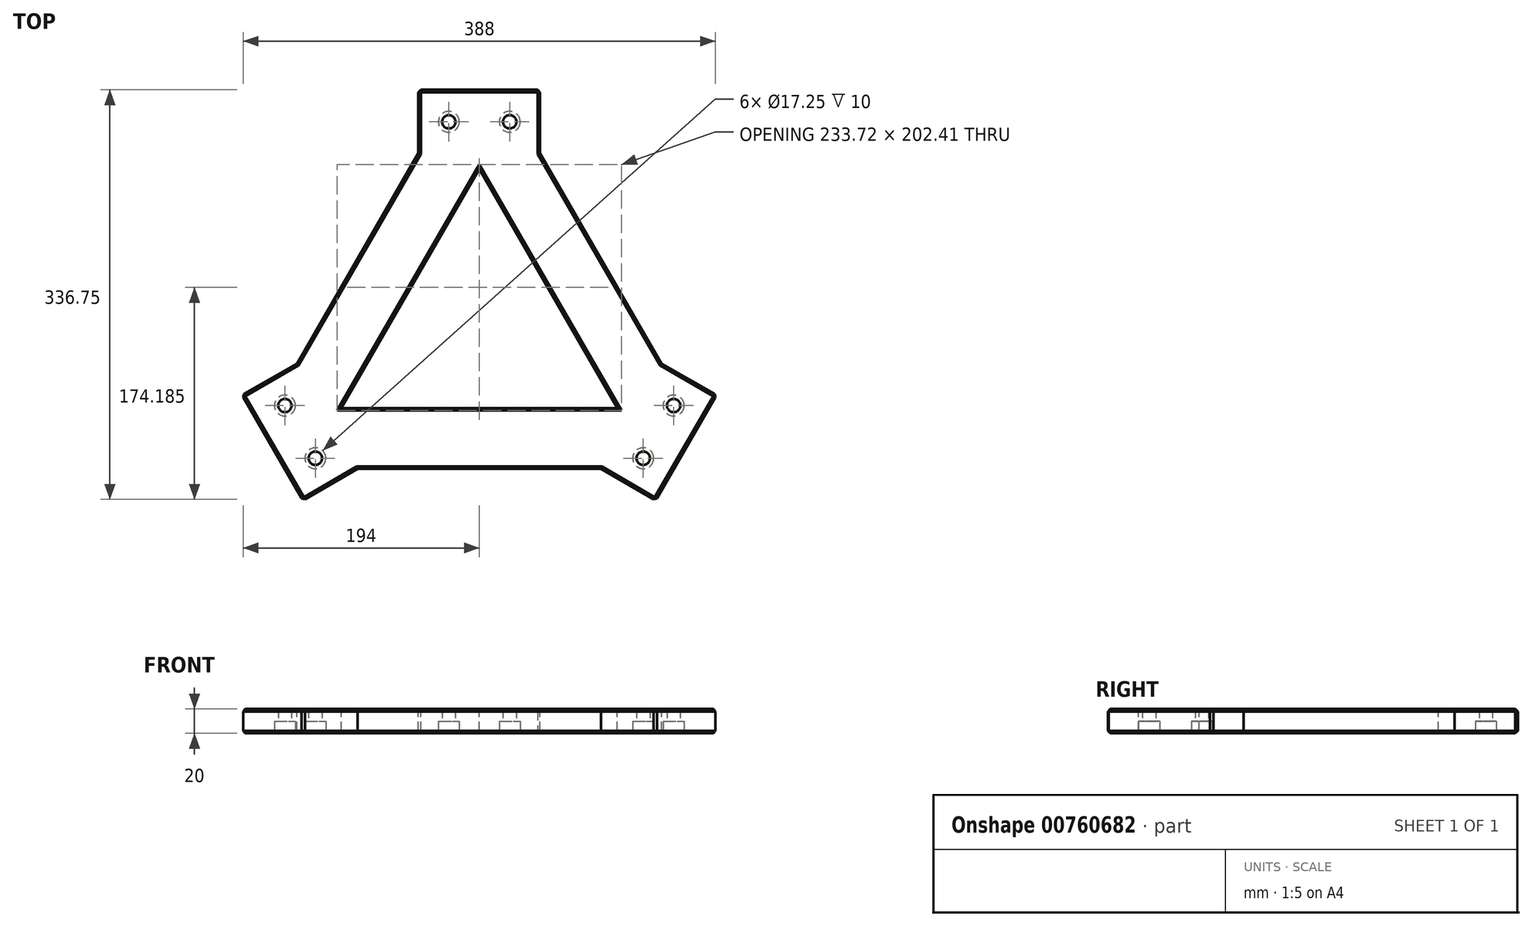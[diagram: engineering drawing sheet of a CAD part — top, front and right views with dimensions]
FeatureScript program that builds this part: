
annotation { "Feature Type Name" : "Feature", "Feature Type Description" : "" }
export const myFeature = defineFeature(function(context is Context, id is Id, definition is map)
    precondition{}
    {
        {
            var Q0;
            Q0=qCreatedBy(makeId("Top.planeOp"),FACE);
            var sketch = newSketch(context, id + "F0", { "sketchPlane" : qUnion([Q0])});
            skLineSegment(sketch, "E0", {"start": v(-200, -115.47) * mm, "end": v(200, -115.47) * mm});
            skLineSegment(sketch, "E1", {"start": v(200, -115.47) * mm, "end": v(0, 230.94) * mm});
            skLineSegment(sketch, "E2", {"start": v(0, 230.94) * mm, "end": v(-200, -115.47) * mm});
            skLineSegment(sketch, "E3", {"start": v(-200, -115.47) * mm, "end": v(100, 57.74) * mm, "construction": true});
            skLineSegment(sketch, "E4", {"start": v(0, 230.94) * mm, "end": v(0, -115.47) * mm, "construction": true});
            skPoint(sketch, "E5", {"position": v(0, 0) * mm});
            skLineSegment(sketch, "E6.0", {"start": v(0, 130.94) * mm, "end": v(-113.4, -65.47) * mm});
            skLineSegment(sketch, "E6.1", {"start": v(113.4, -65.47) * mm, "end": v(0, 130.94) * mm});
            skLineSegment(sketch, "E6.2", {"start": v(-113.4, -65.47) * mm, "end": v(113.4, -65.47) * mm});
            skSolve(sketch);
        }
        {
            var Q0;
            Q0=makeQuery(id+"F0.imprint","IMPRINT",FACE,{"disambiguationData":[TD([[makeQuery(id+"F0.imprint","IMPRINT",EDGE,{"derivedFrom":sQuery(id+"F0.wireOp",EDGE,"E0")}),1.0]])]});
            extrude(context, id + "F1", {"entities" : qUnion([Q0]), "oppositeDirection" : true, "depth" : 20 * mm, "offsetDistance" : 25 * mm});
        }
        {
            var Q0;
            Q0=makeQuery(id+"F1.opExtrude","SWEPT_EDGE",EDGE,{"disambiguationData":[OSD([sQuery(id+"F0.wireOp",EDGE,"E0"),sQuery(id+"F0.wireOp",EDGE,"E2")])]});
            var Q1;
            Q1=makeQuery(id+"F1.opExtrude","SWEPT_EDGE",EDGE,{"disambiguationData":[OSD([sQuery(id+"F0.wireOp",EDGE,"E0"),sQuery(id+"F0.wireOp",EDGE,"E1")])]});
            var Q2;
            Q2=makeQuery(id+"F1.opExtrude","SWEPT_EDGE",EDGE,{"disambiguationData":[OSD([sQuery(id+"F0.wireOp",EDGE,"E1"),sQuery(id+"F0.wireOp",EDGE,"E2")])]});
            chamfer(context, id + "F2", {"entities" : qUnion([Q0, Q1, Q2]), "width" : 40 * mm, "tangentPropagation" : true});
        }
        {
            var Q0;
            Q0=makeQuery(id+"F1.opExtrude","CAP_FACE",FACE,{"disambiguationData":[OSD([sQuery(id+"F0.wireOp",EDGE,"E0"),sQuery(id+"F0.wireOp",EDGE,"E1"),sQuery(id+"F0.wireOp",EDGE,"E2"),sQuery(id+"F0.wireOp",EDGE,"E6.0"),sQuery(id+"F0.wireOp",EDGE,"E6.1"),sQuery(id+"F0.wireOp",EDGE,"E6.2")])],"isStart":true});
            var sketch = newSketch(context, id + "F3", { "sketchPlane" : qUnion([Q0])});
            skLineSegment(sketch, "E7.bottom", {"start": v(-50, 196.3) * mm, "end": v(50, 196.3) * mm});
            skLineSegment(sketch, "E7.top", {"start": v(-50, 144.34) * mm, "end": v(50, 144.34) * mm});
            skLineSegment(sketch, "E7.left", {"start": v(-50, 144.34) * mm, "end": v(-50, 196.3) * mm});
            skLineSegment(sketch, "E7.right", {"start": v(50, 144.34) * mm, "end": v(50, 196.3) * mm});
            skLineSegment(sketch, "E8.1.0", {"start": v(-100, -115.47) * mm, "end": v(-145, -141.45) * mm});
            skLineSegment(sketch, "E8.1.1", {"start": v(-150, -28.87) * mm, "end": v(-195, -54.85) * mm});
            skLineSegment(sketch, "E8.1.2", {"start": v(-100, -115.47) * mm, "end": v(-150, -28.87) * mm});
            skLineSegment(sketch, "E8.1.3", {"start": v(-145, -141.45) * mm, "end": v(-195, -54.85) * mm});
            skLineSegment(sketch, "E8.2.0", {"start": v(150, -28.87) * mm, "end": v(195, -54.85) * mm});
            skLineSegment(sketch, "E8.2.1", {"start": v(100, -115.47) * mm, "end": v(145, -141.45) * mm});
            skLineSegment(sketch, "E8.2.2", {"start": v(150, -28.87) * mm, "end": v(100, -115.47) * mm});
            skLineSegment(sketch, "E8.2.3", {"start": v(195, -54.85) * mm, "end": v(145, -141.45) * mm});
            skPoint(sketch, "E8.center", {"position": v(0, 0) * mm});
            skSolve(sketch);
        }
        {
            var Q0;
            Q0=qSketchRegion(id+"F3",true);
            var Q1;
            Q1=makeQuery(id+"F1.opExtrude","CAP_FACE",FACE,{"disambiguationData":[OSD([sQuery(id+"F0.wireOp",EDGE,"E0"),sQuery(id+"F0.wireOp",EDGE,"E1"),sQuery(id+"F0.wireOp",EDGE,"E2"),sQuery(id+"F0.wireOp",EDGE,"E6.0"),sQuery(id+"F0.wireOp",EDGE,"E6.1"),sQuery(id+"F0.wireOp",EDGE,"E6.2")])],"isStart":false});
            extrude(context, id + "F4", {"entities" : qUnion([Q0]), "operationType" : NewBodyOperationType.ADD, "endBound" : BoundingType.UP_TO_SURFACE, "oppositeDirection" : true, "depth" : 25 * mm, "endBoundEntityFace" : qUnion([Q1]), "offsetDistance" : 25 * mm});
        }
        {
            var Q0;
            {var subQ0=sQuery(id+"F0.wireOp",EDGE,"E6.2");var subQ1=sQuery(id+"F0.wireOp",EDGE,"E6.1");var subQ2=sQuery(id+"F0.wireOp",EDGE,"E6.0");var subQ3=sQuery(id+"F0.wireOp",EDGE,"E2");var subQ4=sQuery(id+"F0.wireOp",EDGE,"E1");var subQ5=sQuery(id+"F0.wireOp",EDGE,"E0");Q0=makeQuery(id+"F4.boolean.opBoolean","MERGE",FACE,{"derivedFrom":[makeQuery(id+"F1.opExtrude","CAP_FACE",FACE,{"disambiguationData":[OSD([subQ5,subQ4,subQ3,subQ2,subQ1,subQ0])],"isStart":false}),makeQuery(id+"F4.opExtrude","CAP_FACE",FACE,{"disambiguationData":[OSD([subQ5,subQ4,subQ3,subQ2,subQ1,subQ0]),OD(0.0)],"isStart":false}),makeQuery(id+"F4.opExtrude","CAP_FACE",FACE,{"disambiguationData":[OSD([subQ5,subQ4,subQ3,subQ2,subQ1,subQ0]),OD(1.0)],"isStart":false}),makeQuery(id+"F4.opExtrude","CAP_FACE",FACE,{"disambiguationData":[OSD([subQ5,subQ4,subQ3,subQ2,subQ1,subQ0]),OD(2.0)],"isStart":false})]});}
            var Q1;
            Q1=makeQuery(id+"F4.boolean.opBoolean","MERGE",FACE,{"derivedFrom":[makeQuery(id+"F1.opExtrude","CAP_FACE",FACE,{"disambiguationData":[OSD([sQuery(id+"F0.wireOp",EDGE,"E0"),sQuery(id+"F0.wireOp",EDGE,"E1"),sQuery(id+"F0.wireOp",EDGE,"E2"),sQuery(id+"F0.wireOp",EDGE,"E6.0"),sQuery(id+"F0.wireOp",EDGE,"E6.1"),sQuery(id+"F0.wireOp",EDGE,"E6.2")])],"isStart":true}),makeQuery(id+"F4.opExtrude","CAP_FACE",FACE,{"disambiguationData":[OSD([sQuery(id+"F3.wireOp",EDGE,"E7.bottom"),sQuery(id+"F3.wireOp",EDGE,"E7.top"),sQuery(id+"F3.wireOp",EDGE,"E7.left"),sQuery(id+"F3.wireOp",EDGE,"E7.right")])],"isStart":true}),makeQuery(id+"F4.opExtrude","CAP_FACE",FACE,{"disambiguationData":[OSD([sQuery(id+"F3.wireOp",EDGE,"E8.1.0"),sQuery(id+"F3.wireOp",EDGE,"E8.1.1"),sQuery(id+"F3.wireOp",EDGE,"E8.1.2"),sQuery(id+"F3.wireOp",EDGE,"E8.1.3")])],"isStart":true}),makeQuery(id+"F4.opExtrude","CAP_FACE",FACE,{"disambiguationData":[OSD([sQuery(id+"F3.wireOp",EDGE,"E8.2.0"),sQuery(id+"F3.wireOp",EDGE,"E8.2.1"),sQuery(id+"F3.wireOp",EDGE,"E8.2.2"),sQuery(id+"F3.wireOp",EDGE,"E8.2.3")])],"isStart":true})]});
            var Q2;
            Q2=makeQuery(id+"F4.opExtrude","SWEPT_EDGE",EDGE,{"disambiguationData":[OSD([sQuery(id+"F3.wireOp",EDGE,"E8.1.0"),sQuery(id+"F3.wireOp",EDGE,"E8.1.3")])]});
            var Q3;
            Q3=makeQuery(id+"F4.opExtrude","SWEPT_EDGE",EDGE,{"disambiguationData":[OSD([sQuery(id+"F3.wireOp",EDGE,"E8.1.1"),sQuery(id+"F3.wireOp",EDGE,"E8.1.3")])]});
            var Q4;
            Q4=makeQuery(id+"F4.opExtrude","SWEPT_EDGE",EDGE,{"disambiguationData":[OSD([sQuery(id+"F3.wireOp",EDGE,"E7.bottom"),sQuery(id+"F3.wireOp",EDGE,"E7.right")])]});
            var Q5;
            Q5=makeQuery(id+"F4.opExtrude","SWEPT_EDGE",EDGE,{"disambiguationData":[OSD([sQuery(id+"F3.wireOp",EDGE,"E7.bottom"),sQuery(id+"F3.wireOp",EDGE,"E7.left")])]});
            var Q6;
            Q6=makeQuery(id+"F4.opExtrude","SWEPT_EDGE",EDGE,{"disambiguationData":[OSD([sQuery(id+"F3.wireOp",EDGE,"E8.2.1"),sQuery(id+"F3.wireOp",EDGE,"E8.2.3")])]});
            var Q7;
            Q7=makeQuery(id+"F4.opExtrude","SWEPT_EDGE",EDGE,{"disambiguationData":[OSD([sQuery(id+"F3.wireOp",EDGE,"E8.2.0"),sQuery(id+"F3.wireOp",EDGE,"E8.2.3")])]});
            chamfer(context, id + "F5", {"entities" : qUnion([Q0, Q1, Q2, Q3, Q4, Q5, Q6, Q7]), "width" : 2 * mm, "tangentPropagation" : true});
        }
        {
            var Q0;
            {var subQ0=sQuery(id+"F0.wireOp",EDGE,"E6.2");var subQ1=sQuery(id+"F0.wireOp",EDGE,"E6.1");var subQ2=sQuery(id+"F0.wireOp",EDGE,"E6.0");var subQ3=sQuery(id+"F0.wireOp",EDGE,"E2");var subQ4=sQuery(id+"F0.wireOp",EDGE,"E1");var subQ5=sQuery(id+"F0.wireOp",EDGE,"E0");Q0=makeQuery(id+"F4.boolean.opBoolean","MERGE",FACE,{"derivedFrom":[makeQuery(id+"F1.opExtrude","CAP_FACE",FACE,{"disambiguationData":[OSD([subQ5,subQ4,subQ3,subQ2,subQ1,subQ0])],"isStart":false}),makeQuery(id+"F4.opExtrude","CAP_FACE",FACE,{"disambiguationData":[OSD([subQ5,subQ4,subQ3,subQ2,subQ1,subQ0]),OD(0.0)],"isStart":false}),makeQuery(id+"F4.opExtrude","CAP_FACE",FACE,{"disambiguationData":[OSD([subQ5,subQ4,subQ3,subQ2,subQ1,subQ0]),OD(1.0)],"isStart":false}),makeQuery(id+"F4.opExtrude","CAP_FACE",FACE,{"disambiguationData":[OSD([subQ5,subQ4,subQ3,subQ2,subQ1,subQ0]),OD(2.0)],"isStart":false})]});}
            var sketch = newSketch(context, id + "F6", { "sketchPlane" : qUnion([Q0])});
            skPoint(sketch, "E9", {"position": v(-25, -170) * mm});
            skPoint(sketch, "E10", {"position": v(25, -170) * mm});
            skLineSegment(sketch, "E11", {"start": v(52.23, -170) * mm, "end": v(-46.28, -170) * mm, "construction": true});
            skLineSegment(sketch, "E12.1.0", {"start": v(121.1, 130.23) * mm, "end": v(170.36, 44.92) * mm, "construction": true});
            skPoint(sketch, "E12.1.1", {"position": v(159.72, 63.35) * mm});
            skPoint(sketch, "E12.1.2", {"position": v(134.72, 106.65) * mm});
            skLineSegment(sketch, "E12.2.0", {"start": v(-173.34, 39.77) * mm, "end": v(-124.09, 125.08) * mm, "construction": true});
            skPoint(sketch, "E12.2.1", {"position": v(-134.72, 106.65) * mm});
            skPoint(sketch, "E12.2.2", {"position": v(-159.72, 63.35) * mm});
            skPoint(sketch, "E12.center", {"position": v(0, 0) * mm});
            skSolve(sketch);
        }
        {
            var Q0;
            Q0=sQuery(id+"F6.wireOp",VERTEX,"E12.1.1");
            var Q1;
            Q1=sQuery(id+"F6.wireOp",VERTEX,"E12.1.2");
            var Q2;
            Q2=sQuery(id+"F6.wireOp",VERTEX,"E9");
            var Q3;
            Q3=sQuery(id+"F6.wireOp",VERTEX,"E10");
            var Q4;
            Q4=sQuery(id+"F6.wireOp",VERTEX,"E12.2.1");
            var Q5;
            Q5=sQuery(id+"F6.wireOp",VERTEX,"E12.2.2");
            var Q6;
            Q6=makeQuery(id+"F1.opExtrude","SWEPT_BODY",BODY,{"disambiguationData":[OSD([sQuery(id+"F0.wireOp",EDGE,"E0"),sQuery(id+"F0.wireOp",EDGE,"E1"),sQuery(id+"F0.wireOp",EDGE,"E2"),sQuery(id+"F0.wireOp",EDGE,"E6.0"),sQuery(id+"F0.wireOp",EDGE,"E6.1"),sQuery(id+"F0.wireOp",EDGE,"E6.2")])]});
            hole(context, id + "F7", {"style" : HoleStyle.C_BORE, "endStyle" : HoleEndStyle.THROUGH, "standardTappedOrClearance" : lookupTablePath({ "standard" : "ISO", "fit" : "Normal", "size" : "M10", "type" : "Clearance" }), "standardBlindInLast" : lookupTablePath({ "fit" : "Standard", "standard" : "ISO", "size" : "M10", "type" : "Clearance" }), "holeDiameter" : 11 * mm, "cBoreDiameter" : 17.25 * mm, "cBoreDepth" : 10 * mm, "majorDiameter" : 5 * mm, "isTappedThrough" : true, "tappedDepth" : 12 * mm, "tapClearance" : 3, "locations" : qUnion([Q0, Q1, Q2, Q3, Q4, Q5]), "scope" : qUnion([Q6])});
        }
    });
